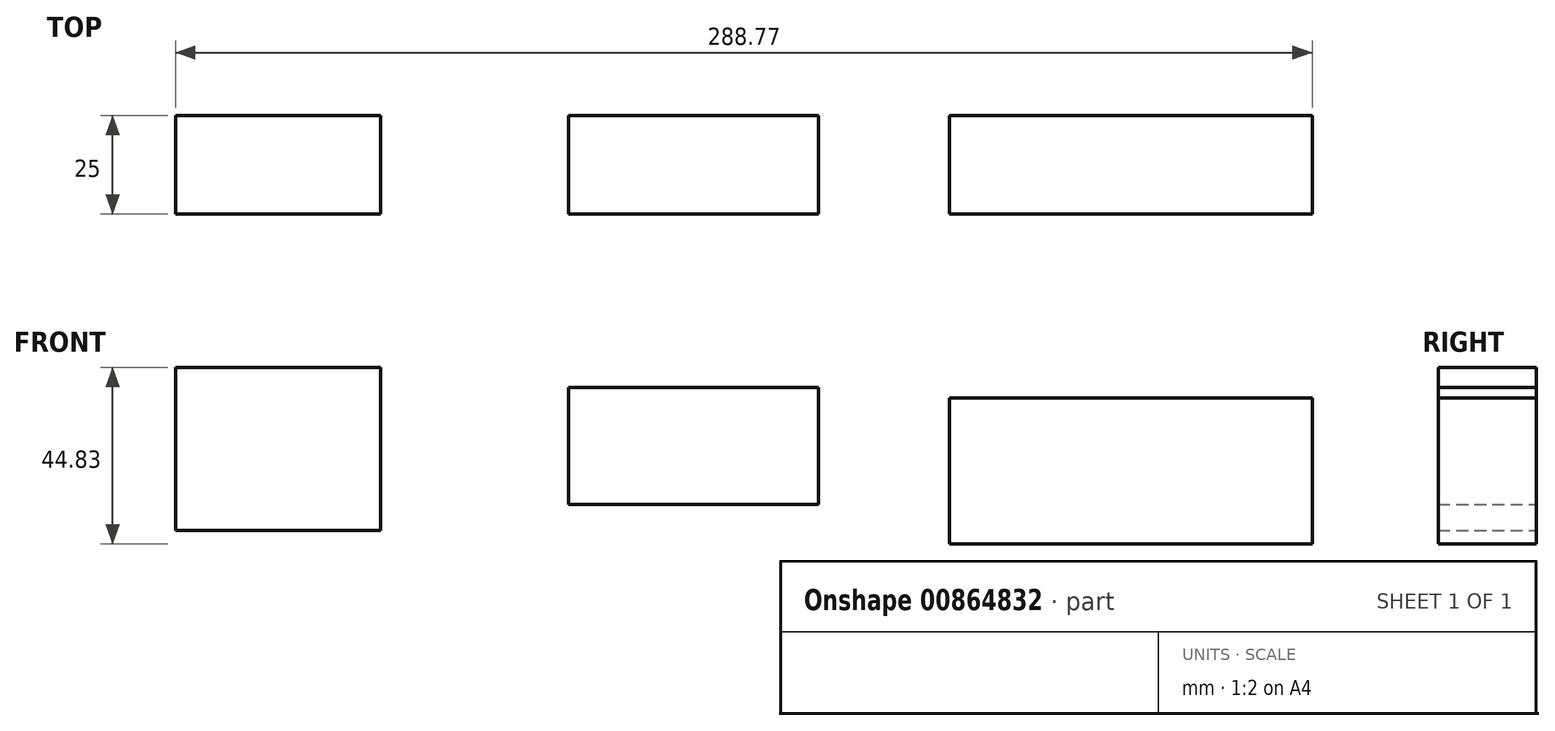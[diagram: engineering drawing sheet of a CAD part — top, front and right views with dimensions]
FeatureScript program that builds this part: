
annotation { "Feature Type Name" : "Feature", "Feature Type Description" : "" }
export const myFeature = defineFeature(function(context is Context, id is Id, definition is map)
    precondition{}
    {
        {
            var Q0;
            Q0=qCreatedBy(makeId("Front.planeOp"),FACE);
            var sketch = newSketch(context, id + "F0", { "sketchPlane" : qUnion([Q0])});
            skLineSegment(sketch, "E0.bottom", {"start": v(-145.73, 44.83) * mm, "end": v(-93.63, 44.83) * mm});
            skLineSegment(sketch, "E0.top", {"start": v(-145.73, 3.4) * mm, "end": v(-93.63, 3.4) * mm});
            skLineSegment(sketch, "E0.left", {"start": v(-145.73, 44.83) * mm, "end": v(-145.73, 3.4) * mm});
            skLineSegment(sketch, "E0.right", {"start": v(-93.63, 44.83) * mm, "end": v(-93.63, 3.4) * mm});
            skLineSegment(sketch, "E1.bottom", {"start": v(-45.89, 39.7) * mm, "end": v(17.65, 39.7) * mm});
            skLineSegment(sketch, "E1.top", {"start": v(-45.89, 9.97) * mm, "end": v(17.65, 9.97) * mm});
            skLineSegment(sketch, "E1.left", {"start": v(-45.89, 39.7) * mm, "end": v(-45.89, 9.97) * mm});
            skLineSegment(sketch, "E1.right", {"start": v(17.65, 39.7) * mm, "end": v(17.65, 9.97) * mm});
            skLineSegment(sketch, "E2.bottom", {"start": v(50.93, 37.06) * mm, "end": v(143.04, 37.06) * mm});
            skLineSegment(sketch, "E2.top", {"start": v(50.93, 0) * mm, "end": v(143.04, 0) * mm});
            skLineSegment(sketch, "E2.left", {"start": v(50.93, 37.06) * mm, "end": v(50.93, 0) * mm});
            skLineSegment(sketch, "E2.right", {"start": v(143.04, 37.06) * mm, "end": v(143.04, 0) * mm});
            skSolve(sketch);
        }
        {
            var Q0;
            Q0 = qSketchRegion(id + "F0", true);
            extrude(context, id + "F1", {"entities" : qUnion([Q0]), "depth" : 25 * mm, "offsetDistance" : 25 * mm});
        }
    });
